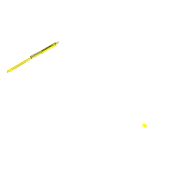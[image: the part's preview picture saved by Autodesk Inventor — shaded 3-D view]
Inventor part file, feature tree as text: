
AUTODESK INVENTOR PART (.ipt)
format: ipt  version: 2022 (Build 260153000, 153)  size: 125,952 bytes
history: native  units: mm
features: sketch x3, extrude x2, projected_geometry x1
ambient origin geometry x8: Origin, YZ Plane, XZ Plane, XY Plane, X Axis, Y Axis, Z Axis, Center Point
bodies: Solid1 (feature_tree)
feature tree (6):
  extrude  "Extrusion1"  Depth=8.0mm
  sketch  "Sketch2"  dims[d2=3.0mm d3=3.0mm]
  extrude  "Extrusion2"  Depth=3.0mm
  sketch  "Sketch1"  dims[d0=270.69mm d1=8.0mm]
  projected_geometry  "Projected Loop1"
  sketch  "Sketch3"  dims[d4=8.0mm d5=0.0mm d10=3.0mm d11=19.5mm d12=80.0mm d13=85.0mm d14=220.0mm d15=700.0mm d16=700.0mm d17=20.0mm d18=0.0mm]
